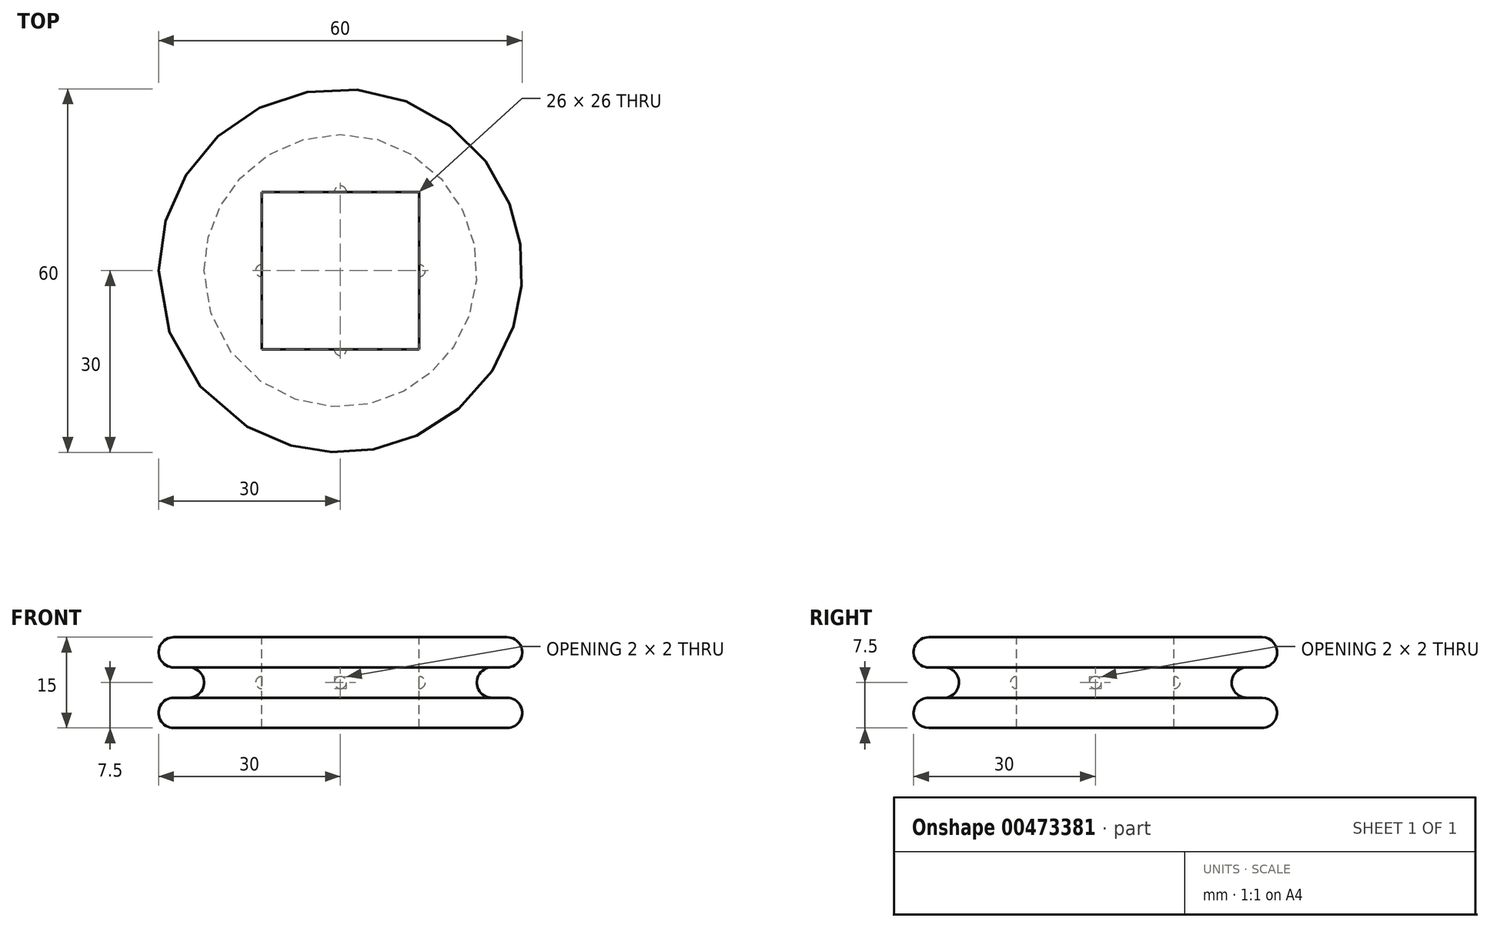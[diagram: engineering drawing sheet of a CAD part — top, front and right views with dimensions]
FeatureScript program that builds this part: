
annotation { "Feature Type Name" : "Feature", "Feature Type Description" : "" }
export const myFeature = defineFeature(function(context is Context, id is Id, definition is map)
    precondition{}
    {
        {
            var Q0;
            Q0=qCreatedBy(makeId("Front.planeOp"),FACE);
            var sketch = newSketch(context, id + "F0", { "sketchPlane" : qUnion([Q0])});
            skLineSegment(sketch, "E0.bottom", {"start": v(0, 0) * mm, "end": v(-27.5, 0) * mm});
            skLineSegment(sketch, "E0.top", {"start": v(0, 15) * mm, "end": v(-27.5, 15) * mm});
            skLineSegment(sketch, "E0.left", {"start": v(0, 0) * mm, "end": v(0, 15) * mm});
            skLineSegment(sketch, "E1", {"start": v(-27.5, 10) * mm, "end": v(-25, 10) * mm});
            skLineSegment(sketch, "E2", {"start": v(-27.5, 5) * mm, "end": v(-25, 5) * mm});
            skArc(sketch, "E3", {"start": v(-25, 5) * mm, "mid": v(-22.5, 7.5) * mm, "end": v(-25, 10) * mm});
            skLineSegment(sketch, "E4", {"start": v(-25, 15) * mm, "end": v(-25, 0) * mm, "construction": true});
            skLineSegment(sketch, "E5", {"start": v(-30, 12.5) * mm, "end": v(20.8, 12.5) * mm, "construction": true});
            skPoint(sketch, "E5.endSnap0", {"position": v(-30, 12.5) * mm});
            skLineSegment(sketch, "E6", {"start": v(-27.5, 15) * mm, "end": v(-25, 15) * mm});
            skLineSegment(sketch, "E7", {"start": v(-27.5, 15) * mm, "end": v(-27.5, 0) * mm, "construction": true});
            skLineSegment(sketch, "E8", {"start": v(-30, 2.5) * mm, "end": v(20.8, 2.5) * mm, "construction": true});
            skArc(sketch, "E9", {"start": v(-27.5, 15) * mm, "mid": v(-30, 12.5) * mm, "end": v(-27.5, 10) * mm});
            skArc(sketch, "E10", {"start": v(-27.5, 5) * mm, "mid": v(-30, 2.5) * mm, "end": v(-27.5, 0) * mm});
            skPoint(sketch, "E11.orphan", {"position": v(-30, 15) * mm});
            skPoint(sketch, "E12.orphan", {"position": v(-30, 10) * mm});
            skPoint(sketch, "E13.orphan", {"position": v(-30, 5) * mm});
            skPoint(sketch, "E14.orphan", {"position": v(-30, 0) * mm});
            skSolve(sketch);
        }
        {
            var Q0;
            Q0=makeQuery(id+"F0.imprint","IMPRINT",FACE,{"disambiguationData":[TD([[makeQuery(id+"F0.imprint","IMPRINT",EDGE,{"derivedFrom":sQuery(id+"F0.wireOp",EDGE,"E0.bottom")}),-1.0]])]});
            var Q1;
            Q1=sQuery(id+"F0.wireOp",EDGE,"E0.left");
            revolve(context, id + "F1", {"entities" : qUnion([Q0]), "axis" : qUnion([Q1]), "revolveType" : RevolveType.FULL});
        }
        {
            var Q0;
            Q0=makeQuery(id+"F1.opRevolve","SWEPT_FACE",FACE,{"disambiguationData":[OSD([sQuery(id+"F0.wireOp",EDGE,"E0.top")])]});
            var sketch = newSketch(context, id + "F2", { "sketchPlane" : qUnion([Q0])});
            skLineSegment(sketch, "E15.bottom", {"start": v(13, -13) * mm, "end": v(-13, -13) * mm});
            skLineSegment(sketch, "E15.top", {"start": v(13, 13) * mm, "end": v(-13, 13) * mm});
            skLineSegment(sketch, "E15.left", {"start": v(13, -13) * mm, "end": v(13, 13) * mm});
            skLineSegment(sketch, "E15.right", {"start": v(-13, -13) * mm, "end": v(-13, 13) * mm});
            skPoint(sketch, "E15.middle", {"position": v(0, 0) * mm});
            skSolve(sketch);
        }
        {
            var Q0;
            Q0 = qSketchRegion(id + "F2", true);
            var Q1;
            Q1=makeQuery(id+"F1.opRevolve","SWEPT_FACE",FACE,{"disambiguationData":[OSD([sQuery(id+"F0.wireOp",EDGE,"E0.bottom")])]});
            extrude(context, id + "F3", {"entities" : qUnion([Q0]), "operationType" : NewBodyOperationType.REMOVE, "endBound" : BoundingType.UP_TO_SURFACE, "oppositeDirection" : true, "endBoundEntityFace" : qUnion([Q1]), "depth" : 25.4 * mm});
        }
        {
            var Q0;
            Q0=qCreatedBy(makeId("Right.planeOp"),FACE);
            var sketch = newSketch(context, id + "F4", { "sketchPlane" : qUnion([Q0])});
            skPoint(sketch, "E16.0", {"position": v(13, 7.5) * mm});
            skArc(sketch, "E17", {"start": v(13, 6.5) * mm, "mid": v(14, 7.5) * mm, "end": v(13, 8.5) * mm});
            skLineSegment(sketch, "E18", {"start": v(13, 8.5) * mm, "end": v(13, 6.5) * mm});
            skSolve(sketch);
        }
        {
            var Q0;
            Q0=makeQuery(id+"F4.imprint","IMPRINT",FACE,{"disambiguationData":[TD([[makeQuery(id+"F4.imprint","IMPRINT",EDGE,{"derivedFrom":sQuery(id+"F4.wireOp",EDGE,"E17")}),1.0]])]});
            var Q1;
            Q1=sQuery(id+"F4.wireOp",EDGE,"E17");
            var Q2;
            Q2=sQuery(id+"F4.wireOp",EDGE,"E18");
            revolve(context, id + "F5", {"entities" : qUnion([Q0]), "surfaceEntities" : qUnion([Q1]), "axis" : qUnion([Q2]), "revolveType" : RevolveType.FULL});
        }
        {
            var Q0;
            Q0=makeQuery(id+"F5.opRevolve","SWEPT_BODY",BODY,{"disambiguationData":[OSD([sQuery(id+"F4.wireOp",EDGE,"E17"),sQuery(id+"F4.wireOp",EDGE,"E18")])]});
            var Q1;
            Q1=sQuery(id+"F0.wireOp",EDGE,"E0.left");
            circularPattern(context, id + "F6", {"operationType" : NewBodyOperationType.REMOVE, "entities" : qUnion([Q0]), "axis" : qUnion([Q1]), "angle" : 360 * degree, "instanceCount" : 4, "equalSpace" : true});
        }
    });
